# Revit family: Mixer_Basin_Abey_PocoK_Tower_FaceBased
name_source: partatom
category: Plumbing Fixtures
units: mm (PartAtom-declared; Revit-internal decimal feet)

## family parameters
Cut with Voids When Loaded = No
Host = Face
OmniClass Number = 23.31.11.19
OmniClass Title = Faucet Mixing Valves
Part Type = Normal
Room Calculation Point = No
Round Connector Dimension = Use Diameter
Shared = No

## types (5) — shared parameters
Assembly Code = C1030210
CW Connection = Yes
Default Elevation = 0 mm
Description = Inspired by the enduring pin-lever design, this elegant tapware delivers a stunning knurled pattern that has been rolled into the material.
HW Connection = Yes
IfcExportAs = IfcValve
IfcExportType = FAUCET
Manufacturer = Abey
ManufacturerOverallDepth = 160 mm
ManufacturerOverallHeight = 273 mm
ManufacturerOverallWidth = 50 mm
ManufacturerURLProductSpecific = https://www.abey.com.au
ModifiedIssue = 20230628 $
URL = https://www.abey.com.au
Uniclass2015Code = Pr_40_20_87_55
Uniclass2015Title = Mixer taps
Uniclass2015Version = Products v1.28
Vent Connection = No
Waste Connection = No
zero-valued in all types: Cost

## per-type parameters (varying)
| type | BodyMaterial | KnurledMaterial | ManufacturerSpecCode | Model | Type Comments |
| Chrome (6B3-K) | Metal_Abey_Chrome | Metal_Abey_Chrome_Knurled | 6B3-K | 6B3-K | Chrome |
| Black (6B3-KB) | Metal_Abey_Black | Metal_Abey_Black_Knurled | 6B3-KB | 6B3-KB | Black |
| Brushed Nickel (6B3-KBN) | Metal_Abey_BrushedNickel | Metal_Abey_BrushedNickel_Knurled | 6B3-KBN | 6B3-KBN | Brushed Nickel |
| Brushed Brass (6B3-KBB) | Metal_Abey_Brass | Metal_Abey_Brass_Knurled | 6B3-KBB | 6B3-KBB | Brushed Brass |
| Gun Metal (6B3-KGM) | Metal_Abey_GunMetal | Metal_Abey_GunMetal_Knurled | 6B3-KGM | 6B3-KGM | Gun Metal |

## geometry (parser evidence)
native form markers: Sweep x5
no freeform markers — native parametric forms only
